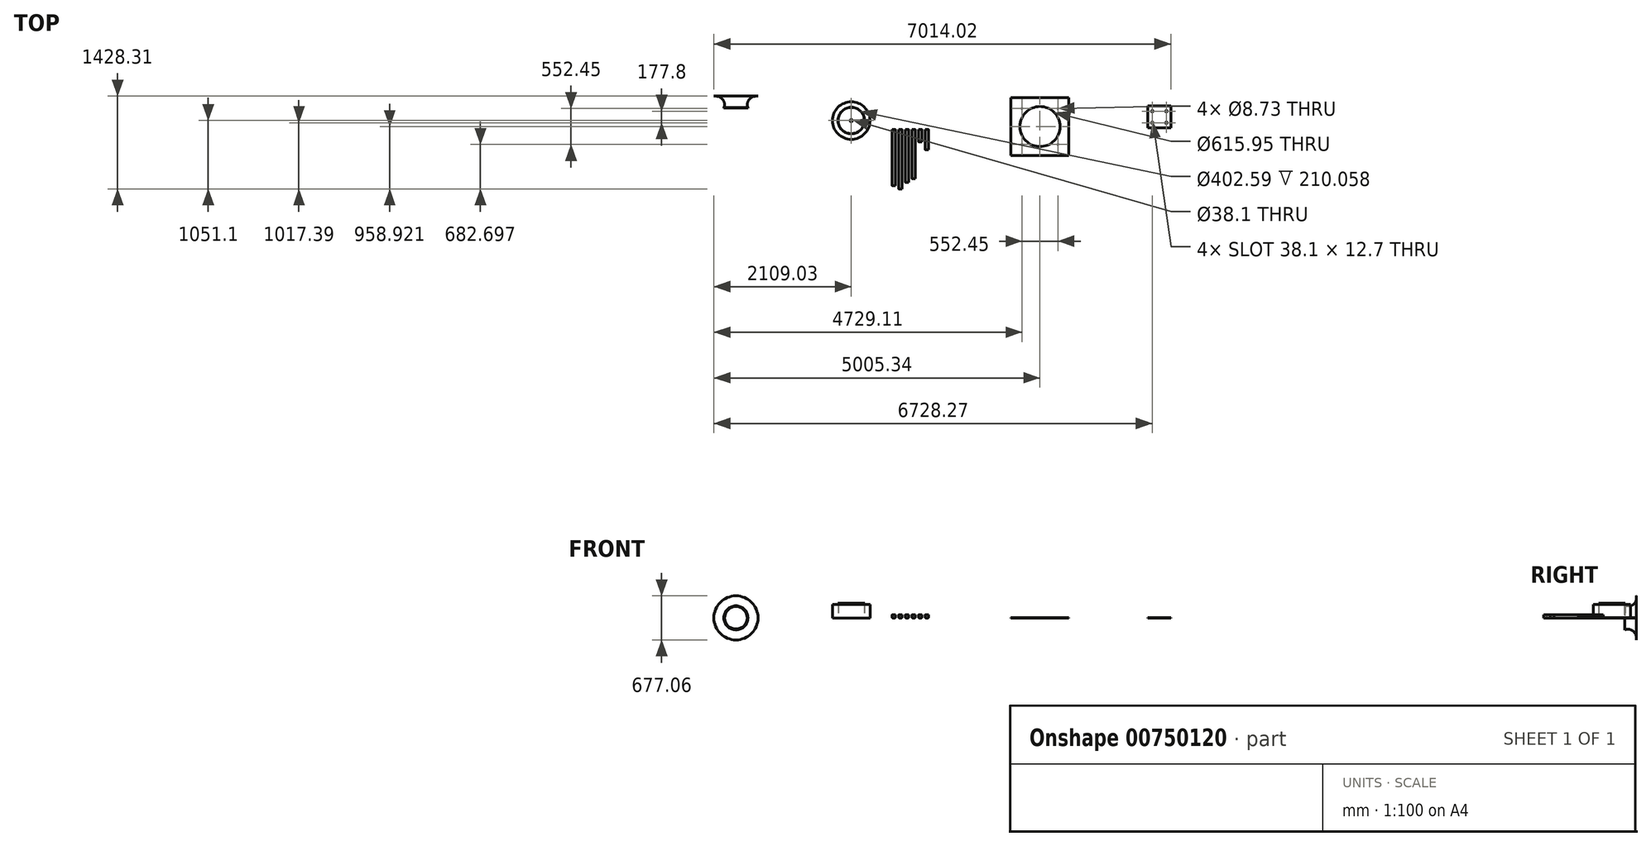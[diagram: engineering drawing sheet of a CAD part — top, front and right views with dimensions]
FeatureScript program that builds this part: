
annotation { "Feature Type Name" : "Feature", "Feature Type Description" : "" }
export const myFeature = defineFeature(function(context is Context, id is Id, definition is map)
    precondition{}
    {
        {
            var Q0;
            Q0=qCreatedBy(makeId("Front.planeOp"),FACE);
            var sketch = newSketch(context, id + "F0", { "sketchPlane" : qUnion([Q0])});
            skLineSegment(sketch, "E0.bottom", {"start": v(0, 0) * mm, "end": v(50.8, 0) * mm});
            skLineSegment(sketch, "E0.top", {"start": v(0, 50.8) * mm, "end": v(50.8, 50.8) * mm});
            skLineSegment(sketch, "E0.left", {"start": v(0, 0) * mm, "end": v(0, 50.8) * mm});
            skLineSegment(sketch, "E0.right", {"start": v(50.8, 0) * mm, "end": v(50.8, 50.8) * mm});
            skLineSegment(sketch, "E1.1.0.0", {"start": v(101.6, 0) * mm, "end": v(101.6, 50.8) * mm});
            skLineSegment(sketch, "E1.1.0.1", {"start": v(101.6, 50.8) * mm, "end": v(152.4, 50.8) * mm});
            skLineSegment(sketch, "E1.1.0.2", {"start": v(152.4, 0) * mm, "end": v(152.4, 50.8) * mm});
            skLineSegment(sketch, "E1.1.0.3", {"start": v(101.6, 0) * mm, "end": v(152.4, 0) * mm});
            skLineSegment(sketch, "E1.2.0.0", {"start": v(203.2, 0) * mm, "end": v(203.2, 50.8) * mm});
            skLineSegment(sketch, "E1.2.0.1", {"start": v(203.2, 50.8) * mm, "end": v(254, 50.8) * mm});
            skLineSegment(sketch, "E1.2.0.2", {"start": v(254, 0) * mm, "end": v(254, 50.8) * mm});
            skLineSegment(sketch, "E1.2.0.3", {"start": v(203.2, 0) * mm, "end": v(254, 0) * mm});
            skLineSegment(sketch, "E1.3.0.0", {"start": v(304.8, 0) * mm, "end": v(304.8, 50.8) * mm});
            skLineSegment(sketch, "E1.3.0.1", {"start": v(304.8, 50.8) * mm, "end": v(355.6, 50.8) * mm});
            skLineSegment(sketch, "E1.3.0.2", {"start": v(355.6, 0) * mm, "end": v(355.6, 50.8) * mm});
            skLineSegment(sketch, "E1.3.0.3", {"start": v(304.8, 0) * mm, "end": v(355.6, 0) * mm});
            skLineSegment(sketch, "E1.4.0.0", {"start": v(406.4, 0) * mm, "end": v(406.4, 50.8) * mm});
            skLineSegment(sketch, "E1.4.0.1", {"start": v(406.4, 50.8) * mm, "end": v(457.2, 50.8) * mm});
            skLineSegment(sketch, "E1.4.0.2", {"start": v(457.2, 0) * mm, "end": v(457.2, 50.8) * mm});
            skLineSegment(sketch, "E1.4.0.3", {"start": v(406.4, 0) * mm, "end": v(457.2, 0) * mm});
            skLineSegment(sketch, "E1.5.0.0", {"start": v(508, 0) * mm, "end": v(508, 50.8) * mm});
            skLineSegment(sketch, "E1.5.0.1", {"start": v(508, 50.8) * mm, "end": v(558.8, 50.8) * mm});
            skLineSegment(sketch, "E1.5.0.2", {"start": v(558.8, 0) * mm, "end": v(558.8, 50.8) * mm});
            skLineSegment(sketch, "E1.5.0.3", {"start": v(508, 0) * mm, "end": v(558.8, 0) * mm});
            skLineSegment(sketch, "E1.6.0.0", {"start": v(609.6, 0) * mm, "end": v(609.6, 50.8) * mm});
            skLineSegment(sketch, "E1.6.0.1", {"start": v(609.6, 50.8) * mm, "end": v(660.4, 50.8) * mm});
            skLineSegment(sketch, "E1.6.0.2", {"start": v(660.4, 0) * mm, "end": v(660.4, 50.8) * mm});
            skLineSegment(sketch, "E1.6.0.3", {"start": v(609.6, 0) * mm, "end": v(660.4, 0) * mm});
            skLineSegment(sketch, "E1.7.0.0", {"start": v(711.2, 0) * mm, "end": v(711.2, 50.8) * mm});
            skLineSegment(sketch, "E1.7.0.1", {"start": v(711.2, 50.8) * mm, "end": v(762, 50.8) * mm});
            skLineSegment(sketch, "E1.7.0.2", {"start": v(762, 0) * mm, "end": v(762, 50.8) * mm});
            skLineSegment(sketch, "E1.7.0.3", {"start": v(711.2, 0) * mm, "end": v(762, 0) * mm});
            skLineSegment(sketch, "E1.8.0.0", {"start": v(812.8, 0) * mm, "end": v(812.8, 50.8) * mm});
            skLineSegment(sketch, "E1.8.0.1", {"start": v(812.8, 50.8) * mm, "end": v(863.6, 50.8) * mm});
            skLineSegment(sketch, "E1.8.0.2", {"start": v(863.6, 0) * mm, "end": v(863.6, 50.8) * mm});
            skLineSegment(sketch, "E1.8.0.3", {"start": v(812.8, 0) * mm, "end": v(863.6, 0) * mm});
            skLineSegment(sketch, "E1.9.0.0", {"start": v(914.4, 0) * mm, "end": v(914.4, 50.8) * mm});
            skLineSegment(sketch, "E1.9.0.1", {"start": v(914.4, 50.8) * mm, "end": v(965.2, 50.8) * mm});
            skLineSegment(sketch, "E1.9.0.2", {"start": v(965.2, 0) * mm, "end": v(965.2, 50.8) * mm});
            skLineSegment(sketch, "E1.9.0.3", {"start": v(914.4, 0) * mm, "end": v(965.2, 0) * mm});
            skLineSegment(sketch, "E1.direction1", {"start": v(0, 0) * mm, "end": v(101.6, 0) * mm, "construction": true});
            skSolve(sketch);
        }
        {
            var Q0;
            Q0=makeQuery(id+"F0.imprint","IMPRINT",FACE,{"disambiguationData":[TD([[makeQuery(id+"F0.imprint","IMPRINT",EDGE,{"derivedFrom":sQuery(id+"F0.wireOp",EDGE,"E0.bottom")}),1.0]])]});
            extrude(context, id + "F1", {"entities" : qUnion([Q0]), "depth" : 863.6 * mm, "offsetDistance" : 25.4 * mm});
        }
        {
            var Q0;
            Q0=makeQuery(id+"F1.opExtrude","SWEPT_EDGE",EDGE,{"disambiguationData":[OSD([sQuery(id+"F0.wireOp",EDGE,"E0.top"),sQuery(id+"F0.wireOp",EDGE,"E0.left")])]});
            var Q1;
            Q1=makeQuery(id+"F1.opExtrude","SWEPT_EDGE",EDGE,{"disambiguationData":[OSD([sQuery(id+"F0.wireOp",EDGE,"E0.bottom"),sQuery(id+"F0.wireOp",EDGE,"E0.left")])]});
            var Q2;
            Q2=makeQuery(id+"F1.opExtrude","SWEPT_EDGE",EDGE,{"disambiguationData":[OSD([sQuery(id+"F0.wireOp",EDGE,"E0.top"),sQuery(id+"F0.wireOp",EDGE,"E0.right")])]});
            var Q3;
            Q3=makeQuery(id+"F1.opExtrude","SWEPT_EDGE",EDGE,{"disambiguationData":[OSD([sQuery(id+"F0.wireOp",EDGE,"E0.bottom"),sQuery(id+"F0.wireOp",EDGE,"E0.right")])]});
            fillet(context, id + "F2", {"entities" : qUnion([Q0, Q1, Q2, Q3]), "radius" : 6.35 * mm, "tangentPropagation" : true, "allowEdgeOverflow" : false});
        }
        {
            var Q0;
            Q0=makeQuery(id+"F0.imprint","IMPRINT",FACE,{"disambiguationData":[TD([[makeQuery(id+"F0.imprint","IMPRINT",EDGE,{"derivedFrom":sQuery(id+"F0.wireOp",EDGE,"E1.1.0.0")}),-1.0]])]});
            extrude(context, id + "F3", {"entities" : qUnion([Q0]), "depth" : 914.4 * mm, "offsetDistance" : 25.4 * mm});
        }
        {
            var Q0;
            Q0=makeQuery(id+"F0.imprint","IMPRINT",FACE,{"disambiguationData":[TD([[makeQuery(id+"F0.imprint","IMPRINT",EDGE,{"derivedFrom":sQuery(id+"F0.wireOp",EDGE,"E1.2.0.0")}),-1.0]])]});
            extrude(context, id + "F4", {"entities" : qUnion([Q0]), "depth" : 812.8 * mm, "offsetDistance" : 25.4 * mm});
        }
        {
            var Q0;
            Q0=makeQuery(id+"F0.imprint","IMPRINT",FACE,{"disambiguationData":[TD([[makeQuery(id+"F0.imprint","IMPRINT",EDGE,{"derivedFrom":sQuery(id+"F0.wireOp",EDGE,"E1.3.0.0")}),-1.0]])]});
            extrude(context, id + "F5", {"entities" : qUnion([Q0]), "depth" : 755.65 * mm, "offsetDistance" : 25.4 * mm});
        }
        {
            var Q0;
            Q0=makeQuery(id+"F0.imprint","IMPRINT",FACE,{"disambiguationData":[TD([[makeQuery(id+"F0.imprint","IMPRINT",EDGE,{"derivedFrom":sQuery(id+"F0.wireOp",EDGE,"E1.4.0.0")}),-1.0]])]});
            extrude(context, id + "F6", {"entities" : qUnion([Q0]), "depth" : 190.5 * mm, "offsetDistance" : 25.4 * mm});
        }
        {
            var Q0;
            Q0=qCreatedBy(makeId("Top.planeOp"),FACE);
            var sketch = newSketch(context, id + "F7", { "sketchPlane" : qUnion([Q0])});
            skCircle(sketch, "E2", {"center": v(-625.3, 136.7) * mm, "radius": 288.3 * mm});
            skCircle(sketch, "E3", {"center": v(-625.3, 136.7) * mm, "radius": 201.3 * mm});
            skCircle(sketch, "E4", {"center": v(-625.3, 136.7) * mm, "radius": 17.46 * mm});
            skSolve(sketch);
        }
        {
            var Q0;
            Q0=makeQuery(id+"F7.imprint","IMPRINT",FACE,{"disambiguationData":[TD([[makeQuery(id+"F7.imprint","IMPRINT",EDGE,{"derivedFrom":sQuery(id+"F7.wireOp",EDGE,"E2")}),1.0]])]});
            extrude(context, id + "F8", {"entities" : qUnion([Q0]), "depth" : 204.98 * mm, "offsetDistance" : 25.4 * mm});
        }
        {
            var Q0;
            Q0=makeQuery(id+"F0.imprint","IMPRINT",FACE,{"disambiguationData":[TD([[makeQuery(id+"F0.imprint","IMPRINT",EDGE,{"derivedFrom":sQuery(id+"F0.wireOp",EDGE,"E1.5.0.0")}),-1.0]])]});
            extrude(context, id + "F9", {"entities" : qUnion([Q0]), "depth" : 311.15 * mm, "offsetDistance" : 25.4 * mm});
        }
        {
            var Q0;
            Q0=qCreatedBy(makeId("Top.planeOp"),FACE);
            var sketch = newSketch(context, id + "F10", { "sketchPlane" : qUnion([Q0])});
            skLineSegment(sketch, "E5.bottom", {"start": v(1826.5, 489.02) * mm, "end": v(2715.5, 489.02) * mm});
            skLineSegment(sketch, "E5.top", {"start": v(1826.5, -399.98) * mm, "end": v(2715.5, -399.98) * mm});
            skLineSegment(sketch, "E5.left", {"start": v(1826.5, 489.02) * mm, "end": v(1826.5, -399.98) * mm});
            skLineSegment(sketch, "E5.right", {"start": v(2715.5, 489.02) * mm, "end": v(2715.5, -399.98) * mm});
            skCircle(sketch, "E6", {"center": v(2271, 44.52) * mm, "radius": 307.98 * mm});
            skPoint(sketch, "E6.centerSnap0", {"position": v(2271, 489.02) * mm});
            skPoint(sketch, "E6.centerSnap1", {"position": v(1826.5, 44.52) * mm});
            skCircle(sketch, "E7", {"center": v(1994.78, -231.7) * mm, "radius": 4.37 * mm});
            skCircle(sketch, "E8", {"center": v(1994.78, 320.75) * mm, "radius": 4.37 * mm});
            skCircle(sketch, "E9", {"center": v(2547.23, 320.75) * mm, "radius": 4.37 * mm});
            skCircle(sketch, "E10", {"center": v(2547.23, -231.7) * mm, "radius": 4.37 * mm});
            skSolve(sketch);
        }
        {
            var Q0;
            Q0=qSketchRegion(id+"F10",true);
            extrude(context, id + "F11", {"entities" : qUnion([Q0]), "depth" : 3.17 * mm, "offsetDistance" : 25.4 * mm});
        }
        {
            var Q0;
            Q0=qCreatedBy(makeId("Top.planeOp"),FACE);
            var sketch = newSketch(context, id + "F12", { "sketchPlane" : qUnion([Q0])});
            skLineSegment(sketch, "E11.bottom", {"start": v(3924.1, 360.16) * mm, "end": v(4279.7, 360.16) * mm});
            skLineSegment(sketch, "E11.top", {"start": v(3924.1, 23.61) * mm, "end": v(4279.7, 23.61) * mm});
            skLineSegment(sketch, "E11.left", {"start": v(3924.1, 360.16) * mm, "end": v(3924.1, 23.61) * mm});
            skLineSegment(sketch, "E11.right", {"start": v(4279.7, 360.16) * mm, "end": v(4279.7, 23.61) * mm});
            skLineSegment(sketch, "E12", {"start": v(3974.9, 309.36) * mm, "end": v(3974.9, 74.41) * mm, "construction": true});
            skLineSegment(sketch, "E13", {"start": v(3974.9, 74.41) * mm, "end": v(4228.9, 74.41) * mm, "construction": true});
            skLineSegment(sketch, "E14", {"start": v(4228.9, 74.41) * mm, "end": v(4228.9, 309.36) * mm, "construction": true});
            skLineSegment(sketch, "E15", {"start": v(4228.9, 309.36) * mm, "end": v(3974.9, 309.36) * mm, "construction": true});
            skLineSegment(sketch, "E16", {"start": v(3993.94, 293.49) * mm, "end": v(3993.94, 268.09) * mm});
            skLineSegment(sketch, "E17", {"start": v(4209.84, 293.49) * mm, "end": v(4209.84, 268.09) * mm});
            skLineSegment(sketch, "E18", {"start": v(3993.94, 115.69) * mm, "end": v(3993.94, 90.29) * mm});
            skLineSegment(sketch, "E19", {"start": v(4209.84, 115.69) * mm, "end": v(4209.84, 90.29) * mm});
            skLineSegment(sketch, "E20", {"start": v(4101.9, 360.16) * mm, "end": v(4101.9, 23.61) * mm, "construction": true});
            skArc(sketch, "E21.0.startCap", {"start": v(3987.6, 293.49) * mm, "mid": v(3993.94, 299.84) * mm, "end": v(4000.3, 293.49) * mm});
            skArc(sketch, "E21.0.endCap", {"start": v(4000.3, 268.09) * mm, "mid": v(3993.94, 261.74) * mm, "end": v(3987.6, 268.09) * mm});
            skLineSegment(sketch, "E21.0.left", {"start": v(4000.3, 293.49) * mm, "end": v(4000.3, 268.09) * mm});
            skLineSegment(sketch, "E21.0.right", {"start": v(3987.6, 293.49) * mm, "end": v(3987.6, 268.09) * mm});
            skArc(sketch, "E21.1.startCap", {"start": v(4203.5, 293.49) * mm, "mid": v(4209.84, 299.84) * mm, "end": v(4216.2, 293.49) * mm});
            skArc(sketch, "E21.1.endCap", {"start": v(4216.2, 268.09) * mm, "mid": v(4209.84, 261.74) * mm, "end": v(4203.5, 268.09) * mm});
            skLineSegment(sketch, "E21.1.left", {"start": v(4216.2, 293.49) * mm, "end": v(4216.2, 268.09) * mm});
            skLineSegment(sketch, "E21.1.right", {"start": v(4203.5, 293.49) * mm, "end": v(4203.5, 268.09) * mm});
            skArc(sketch, "E21.2.startCap", {"start": v(4203.5, 115.69) * mm, "mid": v(4209.84, 122.04) * mm, "end": v(4216.2, 115.69) * mm});
            skArc(sketch, "E21.2.endCap", {"start": v(4216.2, 90.29) * mm, "mid": v(4209.84, 83.94) * mm, "end": v(4203.5, 90.29) * mm});
            skLineSegment(sketch, "E21.2.left", {"start": v(4216.2, 115.69) * mm, "end": v(4216.2, 90.29) * mm});
            skLineSegment(sketch, "E21.2.right", {"start": v(4203.5, 115.69) * mm, "end": v(4203.5, 90.29) * mm});
            skArc(sketch, "E21.3.startCap", {"start": v(3987.6, 115.69) * mm, "mid": v(3993.94, 122.04) * mm, "end": v(4000.3, 115.69) * mm});
            skArc(sketch, "E21.3.endCap", {"start": v(4000.3, 90.29) * mm, "mid": v(3993.94, 83.94) * mm, "end": v(3987.6, 90.29) * mm});
            skLineSegment(sketch, "E21.3.left", {"start": v(4000.3, 115.69) * mm, "end": v(4000.3, 90.29) * mm});
            skLineSegment(sketch, "E21.3.right", {"start": v(3987.6, 115.69) * mm, "end": v(3987.6, 90.29) * mm});
            skPoint(sketch, "E22", {"position": v(4209.84, 280.79) * mm});
            skPoint(sketch, "E23", {"position": v(3993.94, 280.79) * mm});
            skPoint(sketch, "E24", {"position": v(3993.94, 102.99) * mm});
            skPoint(sketch, "E25", {"position": v(4209.84, 102.99) * mm});
            skSolve(sketch);
        }
        {
            var Q0;
            Q0=qSketchRegion(id+"F12",true);
            extrude(context, id + "F13", {"entities" : qUnion([Q0]), "depth" : 6.35 * mm, "offsetDistance" : 25.4 * mm});
        }
        {
            var Q0;
            Q0=makeQuery(id+"F3.opExtrude","SWEPT_EDGE",EDGE,{"disambiguationData":[OSD([sQuery(id+"F0.wireOp",EDGE,"E1.1.0.0"),sQuery(id+"F0.wireOp",EDGE,"E1.1.0.1")])]});
            var Q1;
            Q1=makeQuery(id+"F3.opExtrude","SWEPT_EDGE",EDGE,{"disambiguationData":[OSD([sQuery(id+"F0.wireOp",EDGE,"E1.1.0.1"),sQuery(id+"F0.wireOp",EDGE,"E1.1.0.2")])]});
            var Q2;
            Q2=makeQuery(id+"F4.opExtrude","SWEPT_EDGE",EDGE,{"disambiguationData":[OSD([sQuery(id+"F0.wireOp",EDGE,"E1.2.0.0"),sQuery(id+"F0.wireOp",EDGE,"E1.2.0.1")])]});
            var Q3;
            Q3=makeQuery(id+"F4.opExtrude","SWEPT_EDGE",EDGE,{"disambiguationData":[OSD([sQuery(id+"F0.wireOp",EDGE,"E1.2.0.1"),sQuery(id+"F0.wireOp",EDGE,"E1.2.0.2")])]});
            var Q4;
            Q4=makeQuery(id+"F3.opExtrude","SWEPT_EDGE",EDGE,{"disambiguationData":[OSD([sQuery(id+"F0.wireOp",EDGE,"E1.1.0.0"),sQuery(id+"F0.wireOp",EDGE,"E1.1.0.3")])]});
            var Q5;
            Q5=makeQuery(id+"F3.opExtrude","SWEPT_EDGE",EDGE,{"disambiguationData":[OSD([sQuery(id+"F0.wireOp",EDGE,"E1.1.0.2"),sQuery(id+"F0.wireOp",EDGE,"E1.1.0.3")])]});
            var Q6;
            Q6=makeQuery(id+"F4.opExtrude","SWEPT_EDGE",EDGE,{"disambiguationData":[OSD([sQuery(id+"F0.wireOp",EDGE,"E1.2.0.0"),sQuery(id+"F0.wireOp",EDGE,"E1.2.0.3")])]});
            var Q7;
            Q7=makeQuery(id+"F4.opExtrude","SWEPT_EDGE",EDGE,{"disambiguationData":[OSD([sQuery(id+"F0.wireOp",EDGE,"E1.2.0.2"),sQuery(id+"F0.wireOp",EDGE,"E1.2.0.3")])]});
            var Q8;
            Q8=makeQuery(id+"F5.opExtrude","SWEPT_EDGE",EDGE,{"disambiguationData":[OSD([sQuery(id+"F0.wireOp",EDGE,"E1.3.0.0"),sQuery(id+"F0.wireOp",EDGE,"E1.3.0.3")])]});
            var Q9;
            Q9=makeQuery(id+"F5.opExtrude","SWEPT_EDGE",EDGE,{"disambiguationData":[OSD([sQuery(id+"F0.wireOp",EDGE,"E1.3.0.2"),sQuery(id+"F0.wireOp",EDGE,"E1.3.0.3")])]});
            var Q10;
            Q10=makeQuery(id+"F6.opExtrude","SWEPT_EDGE",EDGE,{"disambiguationData":[OSD([sQuery(id+"F0.wireOp",EDGE,"E1.4.0.0"),sQuery(id+"F0.wireOp",EDGE,"E1.4.0.3")])]});
            var Q11;
            Q11=makeQuery(id+"F6.opExtrude","SWEPT_EDGE",EDGE,{"disambiguationData":[OSD([sQuery(id+"F0.wireOp",EDGE,"E1.4.0.2"),sQuery(id+"F0.wireOp",EDGE,"E1.4.0.3")])]});
            var Q12;
            Q12=makeQuery(id+"F9.opExtrude","SWEPT_EDGE",EDGE,{"disambiguationData":[OSD([sQuery(id+"F0.wireOp",EDGE,"E1.5.0.0"),sQuery(id+"F0.wireOp",EDGE,"E1.5.0.3")])]});
            var Q13;
            Q13=makeQuery(id+"F9.opExtrude","SWEPT_EDGE",EDGE,{"disambiguationData":[OSD([sQuery(id+"F0.wireOp",EDGE,"E1.5.0.2"),sQuery(id+"F0.wireOp",EDGE,"E1.5.0.3")])]});
            var Q14;
            Q14=makeQuery(id+"F5.opExtrude","SWEPT_EDGE",EDGE,{"disambiguationData":[OSD([sQuery(id+"F0.wireOp",EDGE,"E1.3.0.0"),sQuery(id+"F0.wireOp",EDGE,"E1.3.0.1")])]});
            var Q15;
            Q15=makeQuery(id+"F5.opExtrude","SWEPT_EDGE",EDGE,{"disambiguationData":[OSD([sQuery(id+"F0.wireOp",EDGE,"E1.3.0.1"),sQuery(id+"F0.wireOp",EDGE,"E1.3.0.2")])]});
            var Q16;
            Q16=makeQuery(id+"F6.opExtrude","SWEPT_EDGE",EDGE,{"disambiguationData":[OSD([sQuery(id+"F0.wireOp",EDGE,"E1.4.0.0"),sQuery(id+"F0.wireOp",EDGE,"E1.4.0.1")])]});
            var Q17;
            Q17=makeQuery(id+"F6.opExtrude","SWEPT_EDGE",EDGE,{"disambiguationData":[OSD([sQuery(id+"F0.wireOp",EDGE,"E1.4.0.1"),sQuery(id+"F0.wireOp",EDGE,"E1.4.0.2")])]});
            var Q18;
            Q18=makeQuery(id+"F9.opExtrude","SWEPT_EDGE",EDGE,{"disambiguationData":[OSD([sQuery(id+"F0.wireOp",EDGE,"E1.5.0.0"),sQuery(id+"F0.wireOp",EDGE,"E1.5.0.1")])]});
            var Q19;
            Q19=makeQuery(id+"F9.opExtrude","SWEPT_EDGE",EDGE,{"disambiguationData":[OSD([sQuery(id+"F0.wireOp",EDGE,"E1.5.0.1"),sQuery(id+"F0.wireOp",EDGE,"E1.5.0.2")])]});
            fillet(context, id + "F14", {"entities" : qUnion([Q0, Q1, Q2, Q3, Q4, Q5, Q6, Q7, Q8, Q9, Q10, Q11, Q12, Q13, Q14, Q15, Q16, Q17, Q18, Q19]), "radius" : 6.35 * mm, "tangentPropagation" : true, "allowEdgeOverflow" : false});
        }
        {
            var Q0;
            Q0=qCreatedBy(makeId("Top.planeOp"),FACE);
            var sketch = newSketch(context, id + "F15", { "sketchPlane" : qUnion([Q0])});
            skArc(sketch, "E26", {"start": v(-2702.58, 513.9) * mm, "mid": v(-2614.5, 481.2) * mm, "end": v(-2569.12, 398.95) * mm});
            skLineSegment(sketch, "E27", {"start": v(-2702.58, 513.9) * mm, "end": v(-2734.33, 513.9) * mm});
            skArc(sketch, "E28", {"start": v(-2578.53, 332.55) * mm, "mid": v(-2568.99, 365.06) * mm, "end": v(-2569.12, 398.95) * mm});
            skLineSegment(sketch, "E29", {"start": v(-2395.8, 572.97) * mm, "end": v(-2395.8, 297.37) * mm, "construction": true});
            skLineSegment(sketch, "E30", {"start": v(-2569.12, 398.95) * mm, "end": v(-2569.12, 398.95) * mm});
            skArc(sketch, "E31.0", {"start": v(-2580.84, 333.6) * mm, "mid": v(-2571.5, 365.42) * mm, "end": v(-2571.63, 398.57) * mm});
            skArc(sketch, "E31.1", {"start": v(-2702.58, 511.37) * mm, "mid": v(-2616.17, 479.28) * mm, "end": v(-2571.63, 398.57) * mm});
            skLineSegment(sketch, "E32", {"start": v(-2580.84, 333.6) * mm, "end": v(-2580.84, 332.55) * mm});
            skLineSegment(sketch, "E33", {"start": v(-2578.53, 332.55) * mm, "end": v(-2580.84, 332.55) * mm});
            skLineSegment(sketch, "E34", {"start": v(-2702.58, 511.37) * mm, "end": v(-2734.33, 511.37) * mm});
            skLineSegment(sketch, "E35", {"start": v(-2734.33, 511.37) * mm, "end": v(-2734.33, 513.9) * mm});
            skSolve(sketch);
        }
        {
            var Q0;
            Q0 = qSketchRegion(id + "F15", true);
            var Q1;
            Q1=sQuery(id+"F15.wireOp",EDGE,"E29");
            revolve(context, id + "F16", {"surfaceOperationType" : NewSurfaceOperationType.NEW, "entities" : qUnion([Q0]), "axis" : qUnion([Q1]), "revolveType" : RevolveType.FULL});
        }
        {
            var Q0;
            Q0=makeQuery(id+"F8.opExtrude","CAP_FACE",FACE,{"disambiguationData":[OSD([sQuery(id+"F7.wireOp",EDGE,"E2"),sQuery(id+"F7.wireOp",EDGE,"E3")])],"isStart":true});
            var sketch = newSketch(context, id + "F17", { "sketchPlane" : qUnion([Q0])});
            skCircle(sketch, "E36", {"center": v(-625.3, -136.7) * mm, "radius": 201.61 * mm});
            skCircle(sketch, "E37", {"center": v(-625.3, -136.7) * mm, "radius": 19.05 * mm});
            skSolve(sketch);
        }
        {
            var Q0;
            Q0 = qSketchRegion(id + "F17", true);
            extrude(context, id + "F18", {"entities" : qUnion([Q0]), "operationType" : NewBodyOperationType.ADD, "oppositeDirection" : true, "depth" : 12.7 * mm, "offsetDistance" : 25.4 * mm});
        }
        {
            var Q0;
            Q0=makeQuery(id+"F8.opExtrude","CAP_FACE",FACE,{"disambiguationData":[OSD([sQuery(id+"F7.wireOp",EDGE,"E2"),sQuery(id+"F7.wireOp",EDGE,"E3")])],"isStart":false});
            var sketch = newSketch(context, id + "F19", { "sketchPlane" : qUnion([Q0])});
            skCircle(sketch, "E38", {"center": v(-625.3, 136.7) * mm, "radius": 204.47 * mm});
            skSolve(sketch);
        }
        {
            var Q0;
            Q0=makeQuery(id+"F19.imprint","IMPRINT",FACE,{"disambiguationData":[TD([[makeQuery(id+"F19.imprint","IMPRINT",EDGE,{"derivedFrom":sQuery(id+"F19.wireOp",EDGE,"E38")}),1.0]])]});
            extrude(context, id + "F20", {"entities" : qUnion([Q0]), "operationType" : NewBodyOperationType.ADD, "depth" : 17.78 * mm, "offsetDistance" : 25.4 * mm});
        }
    });
